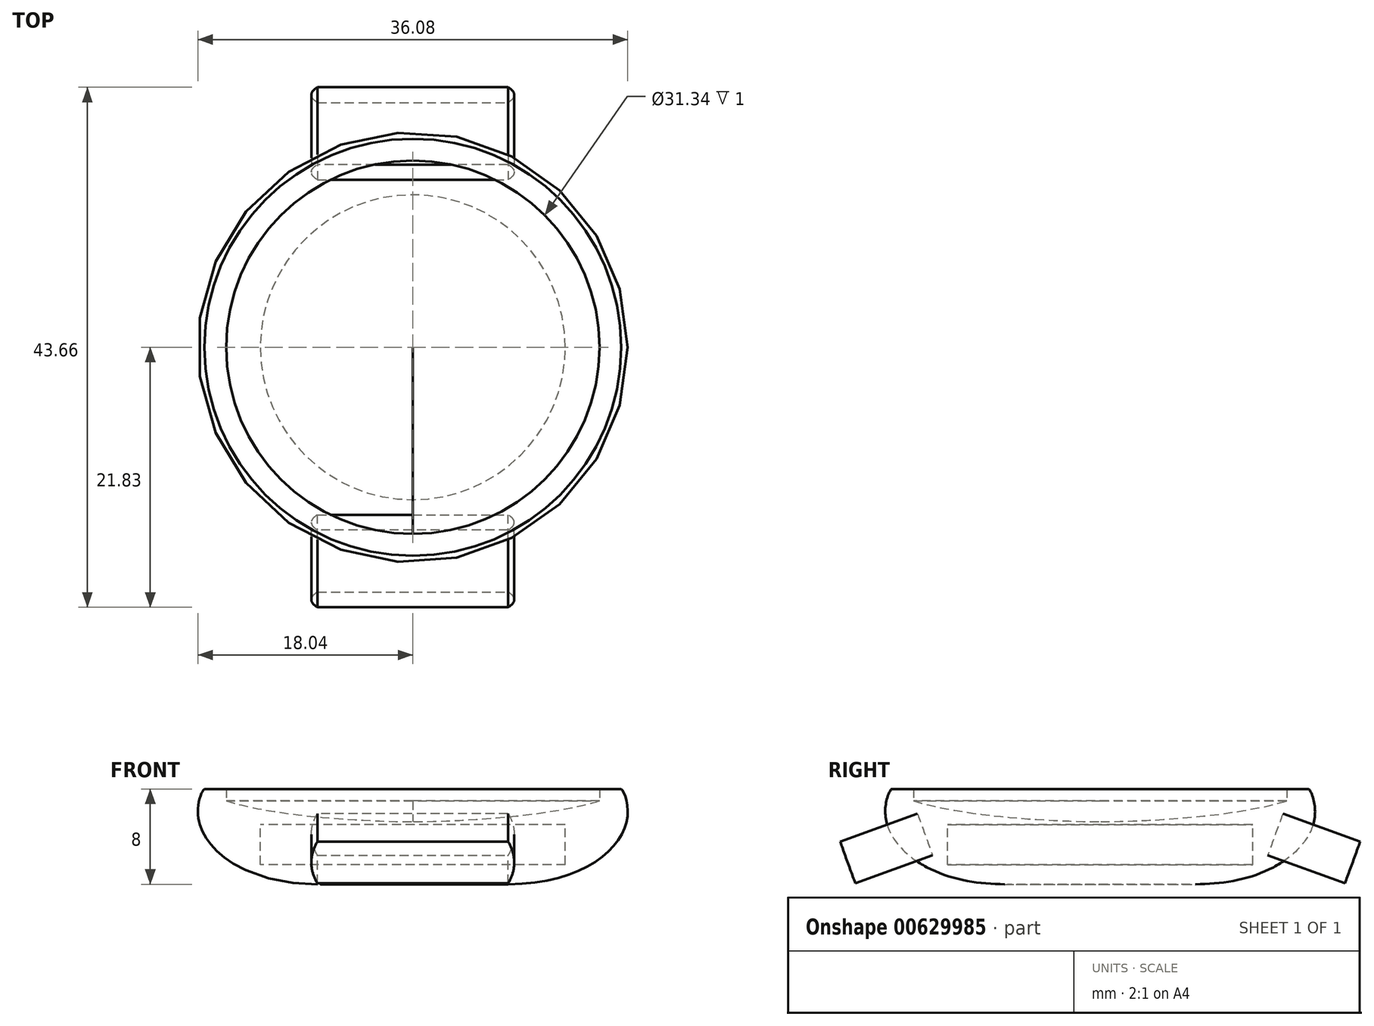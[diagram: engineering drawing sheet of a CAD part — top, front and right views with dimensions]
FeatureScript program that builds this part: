
annotation { "Feature Type Name" : "Feature", "Feature Type Description" : "" }
export const myFeature = defineFeature(function(context is Context, id is Id, definition is map)
    precondition{}
    {
        {
            var Q0;
            Q0=qCreatedBy(makeId("Top.planeOp"),FACE);
            var sketch = newSketch(context, id + "F0", { "sketchPlane" : qUnion([Q0])});
            skCircle(sketch, "E0", {"center": v(0, 0) * mm, "radius": 12.8 * mm});
            skSolve(sketch);
        }
        {
            var Q0;
            Q0 = qSketchRegion(id + "F0", true);
            extrude(context, id + "F1", {"entities" : qUnion([Q0]), "oppositeDirection" : true, "depth" : 3.35 * mm, "offsetDistance" : 25 * mm});
        }
        {
            var Q0;
            Q0=qCreatedBy(makeId("Right.planeOp"),FACE);
            var sketch = newSketch(context, id + "F2", { "sketchPlane" : qUnion([Q0])});
            skLineSegment(sketch, "E1", {"start": v(0, 3) * mm, "end": v(17.5, 3) * mm});
            skLineSegment(sketch, "E2", {"start": v(18, 9) * mm, "end": v(18, -16) * mm, "construction": true});
            skLineSegment(sketch, "E3", {"start": v(0, 20.11) * mm, "end": v(0, -23.68) * mm, "construction": true});
            skLineSegment(sketch, "E4", {"start": v(8, -5) * mm, "end": v(0, -5) * mm});
            skFitSpline(sketch, "E5", {"points": [v(17.5, 3) * mm, v(18, 0.52) * mm, v(8, -5) * mm], "startDerivative": vector(2.08, -1.52) * mm, "endDerivative": vector(-27.52, 0) * mm});
            skLineSegment(sketch, "E6", {"start": v(0, 3) * mm, "end": v(0, -5) * mm});
            skSolve(sketch);
        }
        {
            var Q0;
            Q0=makeQuery(id+"F2.imprint","IMPRINT",FACE,{"disambiguationData":[TD([[makeQuery(id+"F2.imprint","IMPRINT",EDGE,{"derivedFrom":sQuery(id+"F2.wireOp",EDGE,"E1")}),-1.0]])]});
            var Q1;
            Q1=sQuery(id+"F2.wireOp",EDGE,"E3");
            revolve(context, id + "F3", {"entities" : qUnion([Q0]), "axis" : qUnion([Q1]), "revolveType" : RevolveType.FULL});
        }
        {
            var Q0;
            Q0=qCreatedBy(makeId("Right.planeOp"),FACE);
            var sketch = newSketch(context, id + "F4", { "sketchPlane" : qUnion([Q0])});
            skLineSegment(sketch, "E7.0", {"start": v(-15.67, 3) * mm, "end": v(0, 3) * mm});
            skLineSegment(sketch, "E8", {"start": v(-15.67, 3) * mm, "end": v(-15.67, 2) * mm});
            skPoint(sketch, "E9.orphan", {"position": v(-17.5, 3) * mm});
            skFitSpline(sketch, "E10", {"points": [v(-15.67, 2) * mm, v(0, 0.26) * mm], "startDerivative": vector(14.4, -4.39) * mm, "endDerivative": vector(9.36, 0) * mm});
            skLineSegment(sketch, "E11", {"start": v(0, 0) * mm, "end": v(0, -4.57) * mm, "construction": true});
            skLineSegment(sketch, "E12", {"start": v(0, 0.26) * mm, "end": v(0, 3) * mm});
            skPoint(sketch, "E13.orphan", {"position": v(17.5, 3) * mm});
            skSolve(sketch);
        }
        {
            var Q0;
            Q0 = qSketchRegion(id + "F4", true);
            var Q1;
            Q1=sQuery(id+"F4.wireOp",EDGE,"E11");
            revolve(context, id + "F5", {"operationType" : NewBodyOperationType.REMOVE, "entities" : qUnion([Q0]), "axis" : qUnion([Q1]), "revolveType" : RevolveType.FULL, "oppositeDirection" : true});
        }
        {
            var Q0;
            Q0=qCreatedBy(makeId("Top.planeOp"),FACE);
            var sketch = newSketch(context, id + "F6", { "sketchPlane" : qUnion([Q0])});
            skLineSegment(sketch, "E14", {"start": v(-9, 15) * mm, "end": v(12.56, 15) * mm});
            skSolve(sketch);
        }
        {
            var Q0;
            Q0=sQuery(id+"F6.wireOp",EDGE,"E14");
            var Q1;
            Q1=qCreatedBy(makeId("Top.planeOp"),FACE);
            cPlane(context, id + "F7", {"entities" : qUnion([Q0, Q1]), "cplaneType" : CPlaneType.LINE_ANGLE, "offset" : 25 * mm, "angle" : 70 * degree, "width" : 150 * mm, "height" : 150 * mm});
        }
        {
            var Q0;
            Q0=qCreatedBy(id+"F7.planeOp",FACE);
            var sketch = newSketch(context, id + "F8", { "sketchPlane" : qUnion([Q0])});
            skLineSegment(sketch, "E15", {"start": v(0, 6.13) * mm, "end": v(-8, 6.13) * mm});
            skLineSegment(sketch, "E16", {"start": v(0, 2.4) * mm, "end": v(-8, 2.4) * mm});
            skArc(sketch, "E17", {"start": v(-8, 6.13) * mm, "mid": v(-8.51, 4.26) * mm, "end": v(-8, 2.4) * mm});
            skLineSegment(sketch, "E18", {"start": v(0, 10.08) * mm, "end": v(0, -2.76) * mm, "construction": true});
            skArc(sketch, "E19.MirrorCS", {"start": v(8, 6.13) * mm, "mid": v(8.51, 4.26) * mm, "end": v(8, 2.4) * mm});
            skLineSegment(sketch, "E20.MirrorCS", {"start": v(0, 6.13) * mm, "end": v(8, 6.13) * mm});
            skLineSegment(sketch, "E21.MirrorCS", {"start": v(0, 2.4) * mm, "end": v(8, 2.4) * mm});
            skSolve(sketch);
        }
        {
            var Q0;
            Q0 = qSketchRegion(id + "F8", true);
            extrude(context, id + "F9", {"entities" : qUnion([Q0]), "depth" : 6.9 * mm, "offsetDistance" : 25 * mm});
        }
        {
            var Q0;
            Q0=makeQuery(id+"F9.opExtrude","SWEPT_BODY",BODY,{"disambiguationData":[OSD([sQuery(id+"F8.wireOp",EDGE,"E15"),sQuery(id+"F8.wireOp",EDGE,"E16"),sQuery(id+"F8.wireOp",EDGE,"E17"),sQuery(id+"F8.wireOp",EDGE,"E19.MirrorCS"),sQuery(id+"F8.wireOp",EDGE,"E20.MirrorCS"),sQuery(id+"F8.wireOp",EDGE,"E21.MirrorCS")])]});
            var Q1;
            Q1=qCreatedBy(makeId("Front.planeOp"),FACE);
            mirror(context, id + "F10", {"entities" : qUnion([Q0]), "mirrorPlane" : qUnion([Q1])});
        }
    });
